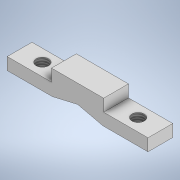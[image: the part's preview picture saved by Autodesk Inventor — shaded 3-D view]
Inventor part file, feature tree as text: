
AUTODESK INVENTOR PART (.ipt)
format: ipt  version: 2022 (Build 260153000, 153)  size: 126,976 bytes
history: native  units: mm
features: extrude x2, thread x2, sketch x2
ambient origin geometry x8: Origin, YZ Plane, XZ Plane, XY Plane, X Axis, Y Axis, Z Axis, Center Point
bodies: Solid1 (feature_tree)
feature tree (6):
  extrude  "Extrusion1"  Depth=6.2mm
  extrude  "Extrusion2"  Depth=22.615mm
  thread  "Thread1"  [1 undecoded]
  thread  "Thread2"  [1 undecoded]
  sketch  "Sketch1"  dims[d0=22.615mm d1=6.2mm]
  sketch  "Sketch2"  dims[d2=26.6mm d3=22.615mm d4=6.2mm d5=22.975mm d9=22.975mm d12=12.64mm d13=0.0mm d14=11.488mm d15=6.18mm d16=6.35mm d17=6.18mm d18=11.488mm d19=6.35mm d20=12.64mm d21=0.0mm d22=6.2mm d23=0.0mm d24=6.2mm d25=0.0mm]
note: 2 required parameter values undecoded (feature->parameter linkage not recoverable at this tier; creation-order binding heuristic only, values carry confidence <= 0.55)
